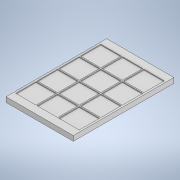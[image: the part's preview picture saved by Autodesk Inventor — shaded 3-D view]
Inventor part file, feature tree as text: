
AUTODESK INVENTOR PART (.ipt)
format: ipt  version: 2020 (Build 240168000, 168)  size: 152,576 bytes
history: native  units: in
note: dims shown in document units (in); Inventor stores cm internally (conversion verified against a paired STEP export)
features: extrude x2, sketch x2, pattern_linear x1
ambient origin geometry x8: Origin, YZ Plane, XZ Plane, XY Plane, X Axis, Y Axis, Z Axis, Center Point
bodies: Solid1 (feature_tree)
feature tree (5):
  extrude  "Extrusion1"  Depth=5.0299in
  extrude  "Extrusion2"  Depth=1.0787in
  pattern_linear  "Rectangular Pattern2"  Spacing1=0.25in  [1 undecoded]
  sketch  "Sketch1"  dims[d0=3.3654in d1=5.0299in]
  sketch  "Sketch3"  dims[d3=45.0deg d4=0.375in d5=0.25in d6=0.0in d23=0.094in d24=0.387in d25=1.0197in d26=1.0197in d27=0.0394in d28=0.0394in d29=0.0394in d30=0.0in d31=1.1811in d33=1.0787in d34=1.5748in d36=1.0787in]
note: 1 required parameter value undecoded (feature->parameter linkage not recoverable at this tier; creation-order binding heuristic only, values carry confidence <= 0.55)
